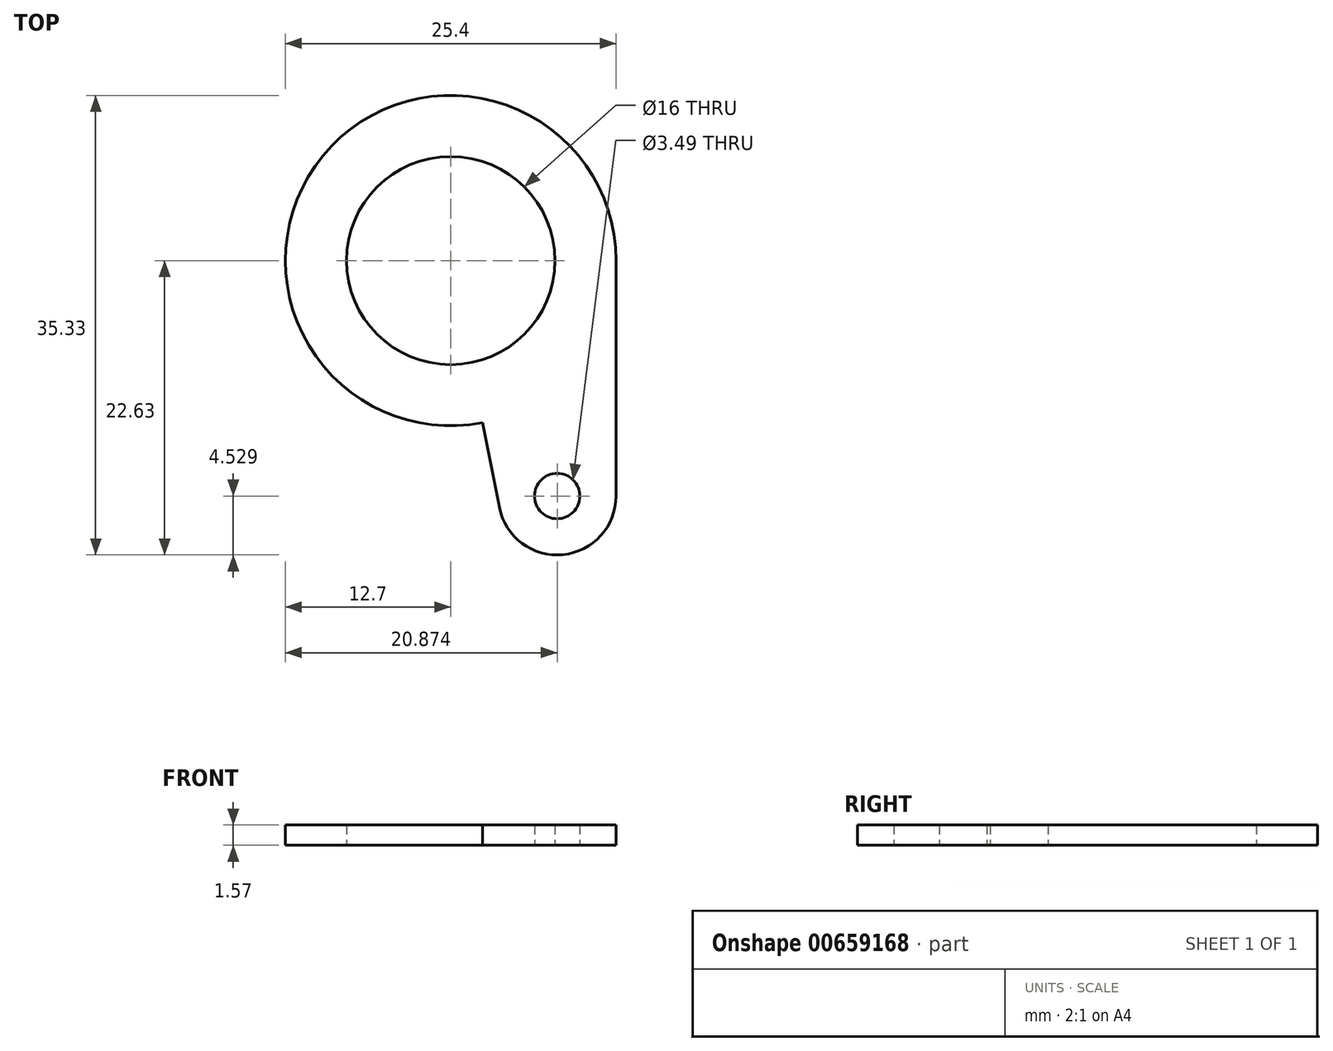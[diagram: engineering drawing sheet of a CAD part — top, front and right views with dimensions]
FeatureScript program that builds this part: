
annotation { "Feature Type Name" : "Feature", "Feature Type Description" : "" }
export const myFeature = defineFeature(function(context is Context, id is Id, definition is map)
    precondition{}
    {
        {
            var Q0;
            Q0=qCreatedBy(makeId("Top.planeOp"),FACE);
            var sketch = newSketch(context, id + "F0", { "sketchPlane" : qUnion([Q0])});
            skCircle(sketch, "E0", {"center": v(0, 0) * mm, "radius": 12.7 * mm});
            skCircle(sketch, "E1", {"center": v(0, 0) * mm, "radius": 8 * mm});
            skLineSegment(sketch, "E2", {"start": v(12.7, 0) * mm, "end": v(12.7, -18.1) * mm});
            skLineSegment(sketch, "E3", {"start": v(0, 0) * mm, "end": v(2.45, -12.46) * mm, "construction": true});
            skPoint(sketch, "E4", {"position": v(12.7, -18.1) * mm});
            skPoint(sketch, "E5", {"position": v(3.73, -18.97) * mm});
            skCircle(sketch, "E6", {"center": v(8.17, -18.1) * mm, "radius": 1.74 * mm});
            skArc(sketch, "E7", {"start": v(12.7, -18.1) * mm, "mid": v(7.74, -13.6) * mm, "end": v(3.73, -18.97) * mm, "construction": true});
            skArc(sketch, "E8", {"start": v(3.73, -18.97) * mm, "mid": v(8.61, -22.6) * mm, "end": v(12.7, -18.1) * mm});
            skLineSegment(sketch, "E9", {"start": v(2.45, -12.46) * mm, "end": v(3.73, -18.97) * mm});
            skSolve(sketch);
        }
        {
            var Q0;
            Q0=makeQuery(id+"F0.imprint","IMPRINT",FACE,{"disambiguationData":[TD([[makeQuery(id+"F0.imprint","IMPRINT",EDGE,{"derivedFrom":sQuery(id+"F0.wireOp",EDGE,"E1")}),-1.0]])]});
            var Q1;
            {var subQ0=sQuery(id+"F0.wireOp",EDGE,"E2");Q1=makeQuery(id+"F0.imprint","IMPRINT",FACE,{"disambiguationData":[TD([[makeQuery(id+"F0.imprint","IMPRINT",EDGE,{"derivedFrom":subQ0}),-1.0]])]});}
            extrude(context, id + "F1", {"entities" : qUnion([Q0, Q1]), "depth" : 1.57 * mm, "offsetDistance" : 25 * mm});
        }
    });
